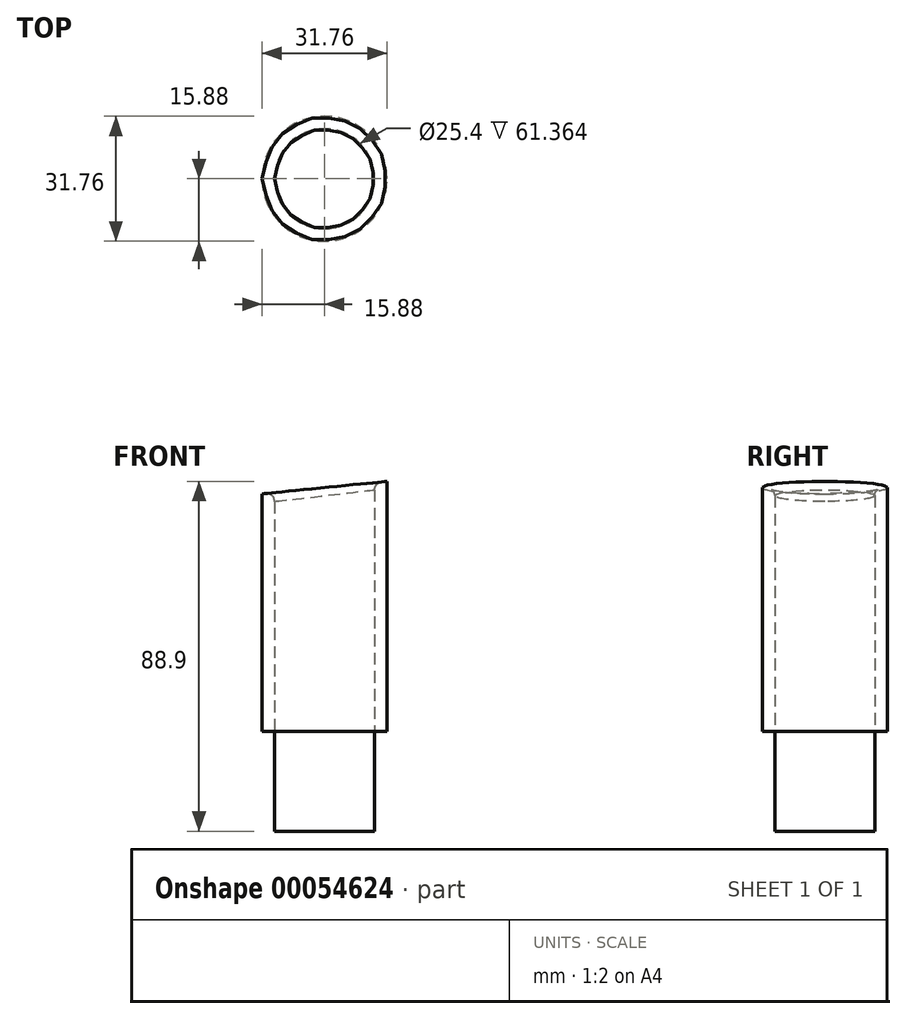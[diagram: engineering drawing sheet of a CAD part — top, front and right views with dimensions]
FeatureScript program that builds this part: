
annotation { "Feature Type Name" : "Feature", "Feature Type Description" : "" }
export const myFeature = defineFeature(function(context is Context, id is Id, definition is map)
    precondition{}
    {
        {
            var Q0;
            Q0=qCreatedBy(makeId("Top.planeOp"),FACE);
            var sketch = newSketch(context, id + "F0", { "sketchPlane" : qUnion([Q0])});
            skCircle(sketch, "E0", {"center": v(0, 0) * mm, "radius": 12.7 * mm});
            skCircle(sketch, "E1.0", {"center": v(0, 0) * mm, "radius": 15.88 * mm});
            skSolve(sketch);
        }
        {
            var Q0;
            Q0=makeQuery(id+"F0.imprint","IMPRINT",FACE,{"disambiguationData":[TD([[makeQuery(id+"F0.imprint","IMPRINT",EDGE,{"derivedFrom":sQuery(id+"F0.wireOp",EDGE,"E0")}),-1.0]])]});
            extrude(context, id + "F1", {"entities" : qUnion([Q0]), "depth" : 76.2 * mm});
        }
        {
            var Q0;
            Q0=makeQuery(id+"F0.imprint","IMPRINT",FACE,{"disambiguationData":[TD([[makeQuery(id+"F0.imprint","IMPRINT",EDGE,{"derivedFrom":sQuery(id+"F0.wireOp",EDGE,"E0")}),1.0]])]});
            extrude(context, id + "F2", {"entities" : qUnion([Q0]), "operationType" : NewBodyOperationType.ADD, "depth" : 3.17 * mm});
        }
        {
            var Q0;
            Q0=qCreatedBy(makeId("Front.planeOp"),FACE);
            var sketch = newSketch(context, id + "F3", { "sketchPlane" : qUnion([Q0])});
            skLineSegment(sketch, "E2.bottom", {"start": v(0, 0) * mm, "end": v(15.87, 0) * mm, "construction": true});
            skLineSegment(sketch, "E2.top", {"start": v(0, 76.2) * mm, "end": v(15.87, 76.2) * mm, "construction": true});
            skLineSegment(sketch, "E2.left", {"start": v(0, 0) * mm, "end": v(0, 76.2) * mm, "construction": true});
            skLineSegment(sketch, "E2.right", {"start": v(15.87, 0) * mm, "end": v(15.87, 76.2) * mm, "construction": true});
            skLineSegment(sketch, "E3.MirrorCS", {"start": v(0, 76.2) * mm, "end": v(-15.87, 76.2) * mm, "construction": true});
            skLineSegment(sketch, "E4.MirrorCS", {"start": v(-15.87, 0) * mm, "end": v(-15.87, 76.2) * mm, "construction": true});
            skLineSegment(sketch, "E5", {"start": v(15.87, 76.2) * mm, "end": v(-15.88, 73.03) * mm});
            skLineSegment(sketch, "E6", {"start": v(-15.87, 73.03) * mm, "end": v(-15.87, 76.2) * mm});
            skLineSegment(sketch, "E7", {"start": v(-15.87, 76.2) * mm, "end": v(15.87, 76.2) * mm});
            skSolve(sketch);
        }
        {
            var Q0;
            Q0 = qSketchRegion(id + "F3", true);
            extrude(context, id + "F4", {"entities" : qUnion([Q0]), "operationType" : NewBodyOperationType.REMOVE, "endBound" : BoundingType.SYMMETRIC, "depth" : 38.1 * mm});
        }
        {
            var Q0;
            Q0=makeQuery(id+"F4.boolean.opBoolean","INTERSECT",EDGE,{"derivedFrom":[makeQuery(id+"F1.opExtrude","SWEPT_FACE",FACE,{"disambiguationData":[OSD([sQuery(id+"F0.wireOp",EDGE,"E0")])]}),makeQuery(id+"F4.opExtrude","SWEPT_FACE",FACE,{"disambiguationData":[OSD([sQuery(id+"F3.wireOp",EDGE,"E5")])]})]});
            fillet(context, id + "F5", {"entities" : qUnion([Q0]), "radius" : 2.03 * mm, "tangentPropagation" : true, "allowEdgeOverflow" : false});
        }
        {
            var Q0;
            {var subQ0=sQuery(id+"F0.wireOp",EDGE,"E0");Q0=makeQuery(id+"F2.boolean.opBoolean","MERGE",FACE,{"derivedFrom":[makeQuery(id+"F1.opExtrude","CAP_FACE",FACE,{"disambiguationData":[OSD([subQ0,sQuery(id+"F0.wireOp",EDGE,"E1.0")])],"isStart":true}),makeQuery(id+"F2.opExtrude","CAP_FACE",FACE,{"disambiguationData":[OSD([subQ0])],"isStart":true})]});}
            extrude(context, id + "F6", {"entities" : qUnion([Q0]), "operationType" : NewBodyOperationType.REMOVE, "oppositeDirection" : true, "depth" : 12.7 * mm});
        }
        {
            var Q0;
            Q0=makeQuery(id+"F0.imprint","IMPRINT",FACE,{"disambiguationData":[TD([[makeQuery(id+"F0.imprint","IMPRINT",EDGE,{"derivedFrom":sQuery(id+"F0.wireOp",EDGE,"E0")}),1.0]])]});
            extrude(context, id + "F7", {"entities" : qUnion([Q0]), "operationType" : NewBodyOperationType.ADD, "endBound" : BoundingType.SYMMETRIC, "depth" : 25.4 * mm});
        }
    });
